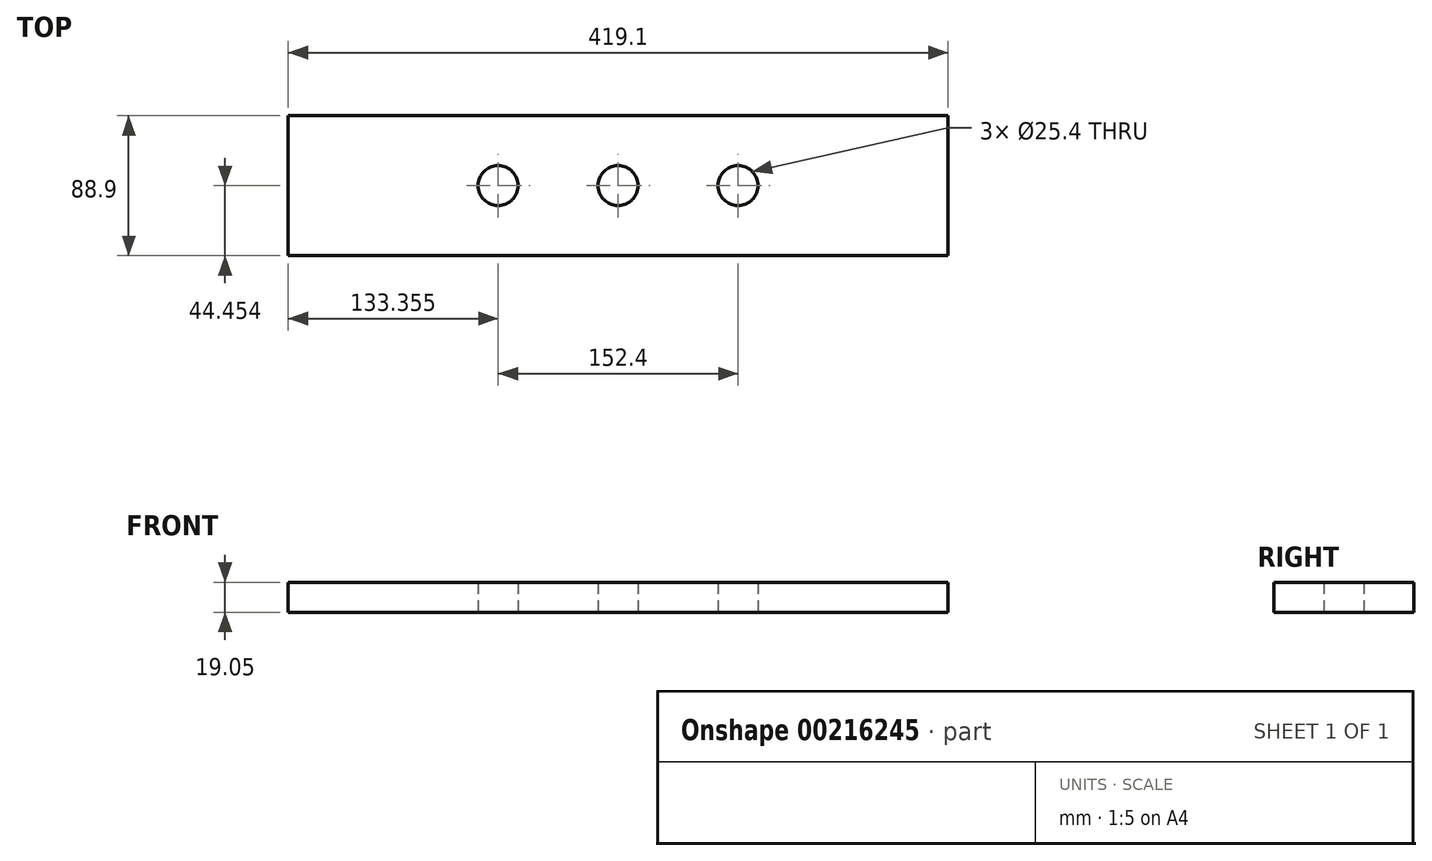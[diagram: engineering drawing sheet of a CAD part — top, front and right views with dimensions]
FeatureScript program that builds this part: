
annotation { "Feature Type Name" : "Feature", "Feature Type Description" : "" }
export const myFeature = defineFeature(function(context is Context, id is Id, definition is map)
    precondition{}
    {
        {
            var Q0;
            Q0=qCreatedBy(makeId("Top.planeOp"),FACE);
            var sketch = newSketch(context, id + "F0", { "sketchPlane" : qUnion([Q0])});
            skLineSegment(sketch, "E0", {"start": v(-3202.89, -858.57) * mm, "end": v(-2783.79, -858.57) * mm});
            skLineSegment(sketch, "E1", {"start": v(-2783.79, -858.57) * mm, "end": v(-2783.79, -769.67) * mm});
            skLineSegment(sketch, "E2", {"start": v(-2783.79, -769.67) * mm, "end": v(-3202.89, -769.67) * mm});
            skLineSegment(sketch, "E3", {"start": v(-3202.89, -769.67) * mm, "end": v(-3202.89, -858.57) * mm});
            skCircle(sketch, "E4", {"center": v(-2993.34, -814.12) * mm, "radius": 12.7 * mm});
            skCircle(sketch, "E5", {"center": v(-2917.14, -814.12) * mm, "radius": 12.7 * mm});
            skCircle(sketch, "E6", {"center": v(-3069.54, -814.12) * mm, "radius": 12.7 * mm});
            skSolve(sketch);
        }
        {
            var Q0;
            Q0=makeQuery(id+"F0.imprint","IMPRINT",FACE,{"disambiguationData":[TD([[makeQuery(id+"F0.imprint","IMPRINT",EDGE,{"derivedFrom":sQuery(id+"F0.wireOp",EDGE,"E0")}),1.0]])]});
            extrude(context, id + "F1", {"entities" : qUnion([Q0]), "depth" : 19.05 * mm});
        }
    });
